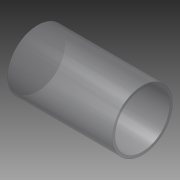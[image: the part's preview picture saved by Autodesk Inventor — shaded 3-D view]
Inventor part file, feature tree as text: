
AUTODESK INVENTOR PART (.ipt)
format: ipt  version: 2015 (Build 190159000, 159)  size: 103,424 bytes
history: native  units: mm
features: extrude x1, sketch x1
ambient origin geometry x8: Origin, YZ Plane, XZ Plane, XY Plane, X Axis, Y Axis, Z Axis, Center Point
bodies: Solid1 (feature_tree)
feature tree (2):
  extrude  "Extrusion1"  Depth=180.0mm
  sketch  "Sketch1"  dims[d0=103.0mm d2=94.0mm d3=180.0mm d4=0.0mm]
